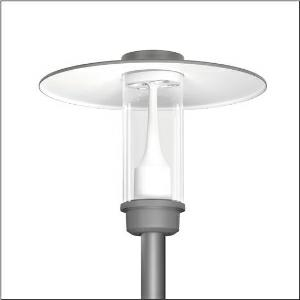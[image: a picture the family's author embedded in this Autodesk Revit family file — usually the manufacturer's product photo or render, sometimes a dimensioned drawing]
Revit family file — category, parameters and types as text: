
# Revit family: litepole_2_iq___st1_2a_5xa5425ef14h_fad6
name_source: partatom
category: Lighting Fixtures
units: mm (PartAtom-declared; Revit-internal decimal feet)

## family parameters
Cut with Voids When Loaded = No
Host = Face
Light Source = No
Part Type = Normal
Room Calculation Point = No
Round Connector Dimension = Use Diameter
Shared = No

## types (1)
- --- (1 x LED, 1550 lm, 10.5 W, 3000K)
    Apparent Load = 11 VA
    CIE Flux Codes = 22 60 92 98 100
    Color Rendering = 70
    Color Temperature = 3000K
    Default Elevation = 1800 mm
    Description = Litepole 2 iQ, mast luminaire, Module 540 iQ-SR, primary light control with 3 zone facetted reflector, of plastic, silver coated, highly specular, structured, primary optical cover: cover, of PMMA, transparent, light distribution: ST1.2a, light emission: direct distribution, primary light characteristic: asymmetric, installation type: post-top, LED, High Power LED, rated luminous flux: 1.550lm, luminous efficacy: 148lm/W, light colour: 730, colour temperature: 3000K, control gear: iQ Street-Remote, control: Auto-Match, Temp-Guard, Lumen-Switch, Night-Set, Smart-Wire, Light-Fading, Desk-Remote (wireless, voltage-free reading and setting of iQ features in the workshop via application-optimized NFC function/RFID function), optimised constant luminous flux control (CLO 2.0), Street-Remote, pre-setting: logarithmic dimming characteristic, with terminal, 6-pole, max. 2.5mm², mains connection: 230..240V, AC, 50/60Hz, start of lifetime: 11W, end of service life: 11W, reduction: 5W, luminaire housing, upper part, of aluminium, coated, Siteco® metallic grey (DB 702S), diameter: 750mm, height: 590mm, spigot size: d x l = 76 x 70mm (post-top) | with reducer (optional accessory) 60 x 70mm, mounting height: 3..5m, post-top mast mounting element, of diecast aluminium, coated, Siteco® metallic grey (DB 702S), Module 540 iQ-SR, traffic white (RAL 9016), equipment: standard, protection rating (complete): IP65, insulation class (complete): insulation class II (safety insulation), certification: CE, ENEC, VDE, packaging unit: 1 piece

Light Distribution: ST1.2a
    Height = 590 mm
    Lamp = 1 x LED
    Lamp Light Flux = 1550 lm
    Lamp Power = 10.5 W
    Lamp count = 1
    Length = 750 mm
    Luminous efficacy = 148 lm/W
    Manufacturer = Siteco
    ModVariant = No
    Model = 5XA5425EF14H
    Number of Poles = 1
    OnlyDefault = Yes
    Power Factor = 1
    Product Name = Litepole 2 iQ | ST1.2a
    Product group = mast luminaire | pylon top
    ProductGroupID = 6100
    Protection Class = Protection class II
    Protection Degree = IP 65
    RLX_Detail_Level = 1
    RLX_Emergency_Light_Flux = 0 lm
    RLX_Emergency_Type = 0
    RLX_Emergency_Type_DB = No
    RlxData = <blob elided: 63545 chars, md5=725c5ca9>
    Socket = socket
    Standby Power = 0 W
    System Light Flux = 1550 lm
    System Power = 11 W
    Type Comments = factory setting: luminous flux: 100 % | dim-lin: 254 | 419 mA
    Type Image = l_1006518.jpg
    URL = http://relux.com
    VarID = @adj_213943
    Voltage = 0 V
    Weight = 0.00 kg
    Width = 0 mm  [stored 0 ft]

note: [stored X ft] marks values corroborated as IEEE doubles in the binary element streams (Revit-internal decimal feet)

## geometry (parser evidence)
native form markers: Blend x4, Sweep x10
no freeform markers — native parametric forms only
